# Revit family: JASMIN oprawa ścienna
name_source: partatom
category: Lighting Fixtures
revit_build: Autodesk Revit Architecture 2015 (Build: 20140322_1515(x64)
units: mm (PartAtom-declared; Revit-internal decimal feet)

## types (3) — shared parameters
Apparent Load = 60 VA
Color Filter = 16777215
Dimming Lamp Color Temperature Shift = <None>
Długość = 407 mm
IP = IP20
Klasyfikacja obciążenia = Oświetlenie
Manufacturer = KANLUX
Materiał klosz = KANLUX - klosz - szkło satynowe
Moc oprawy = 60 W
Photometric Web File = generic
Szerokość = 116 mm
Tilt Angle = 90.00°
Wattage Comments = 60
Współczynnik mocy = 1
Wysokość = 76 mm
zero-valued in all types: Default Elevation

## per-type parameters (varying)
| type | Kod | Materiał obudowa | Model | URL |
| KANLUX JASMIN oprawa ścienna W-W 23757 biały dab | 23757 | KANLUX - obudowa - biały dąb | JASMIN W-W | www.kanlux.pl |
| KANLUX JASMIN oprawa ścienna WE-W 23756 wenge | 23756 | KANLUX - obudowa - wenge | JASMIN WE-W | www.kanlux.pl |
| KANLUX JASMIN oprawa ścienna W/M-W 23758 biały | 23758 | KANLUX - obudowa - biały | JASMIN W/M-W | www.kanlux.pl/pl |
